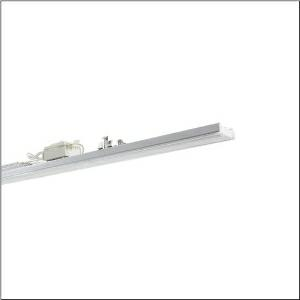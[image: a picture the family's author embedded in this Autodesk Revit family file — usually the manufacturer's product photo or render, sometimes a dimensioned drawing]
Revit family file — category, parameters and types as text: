
# Revit family: licross_r__21_recessed_mo_52tl117n485g_e718
name_source: partatom
category: Lighting Fixtures
units: mm (PartAtom-declared; Revit-internal decimal feet)

## family parameters
Cut with Voids When Loaded = No
Host = Face
Light Source = No
Part Type = Normal
Room Calculation Point = No
Round Connector Dimension = Use Diameter
Shared = No

## types (1)
- Licross® 21 Recessed MO (1 x LED, 8680 lm, 47.9 W, 4000K)
    Apparent Load = 48 VA
    CIE Flux Codes = 89 96 99 100 100
    Color Rendering = 80
    Color Temperature = 4000K
    Default Elevation = 1800 mm
    Description = Licross® 21 Recessed MO, luminaire insert, of sheet steel, galvanised, coil coated, white, length: 1.500mm, width: 66mm, height: 67mm, LED rated luminous flux: 8.680lm, light colour: 840, control gear: ON/OFF, with plug, 3-pole, with phase selection, mains connection: 220..240V, AC, 50/60Hz, rated input power: 48W, internal wiring halogen-free, primary light control with lens, of plastic, primary optical cover: cover, of PMMA, light emission: direct distribution, primary light characteristic: symmetric, protection rating (complete): IP40, insulation class (complete): insulation class I (protective earthing), certification: CE, ENEC, VDE, UKCA, protection symbol: D if used in an environment without relevant dust loads with corresponding accessories, impact resistance: IK06, permissible ambient temperature for indoor applications: -35..+40°C, corresponds to IFS (International Featured Standards) requirements for safety and quality in the food industry, reducing of maximum allowable ambient temperature of 5°C with ceiling mounting, LABS conformity tested according to VDMA 24364:2018-05, packaging unit: 1 piece
    Height = 58 mm
    Lamp = 1 x LED
    Lamp Light Flux = 8680 lm
    Lamp Power = 47.9 W
    Lamp count = 1
    Length = 1500 mm
    Luminous efficacy = 181 lm/W
    Manufacturer = Siteco
    ModVariant = No
    Model = 52TL117N485G
    Mounting Place = Ceiling
    Mounting Type = Pendant
    Number of Poles = 1
    OnlyDefault = Yes
    Power Factor = 1
    Product Name = Licross® 21 Recessed MO
    Product group = luminaire insert | ceiling pendant
    ProductGroupID = 902
    Protection Class = Protection class I
    Protection Degree = IP 40
    RLX_Detail_Level = 1
    RLX_Emergency_Light_Flux = 0 lm
    RLX_Emergency_Type = 0
    RLX_Emergency_Type_DB = No
    RlxData = <blob elided: 20885 chars, md5=20043200>
    Socket = socket
    Standby Power = 0 W
    System Light Flux = 8680 lm
    System Power = 48 W
    Type Comments = Product without accessories
    Type Image = l_1296930.jpg
    URL = http://relux.com
    VarID = ---
    Voltage = 0 V
    Weight = 0.00 kg
    Width = 66 mm

## geometry (parser evidence)
native form markers: Blend x4, Sweep x11
no freeform markers — native parametric forms only
